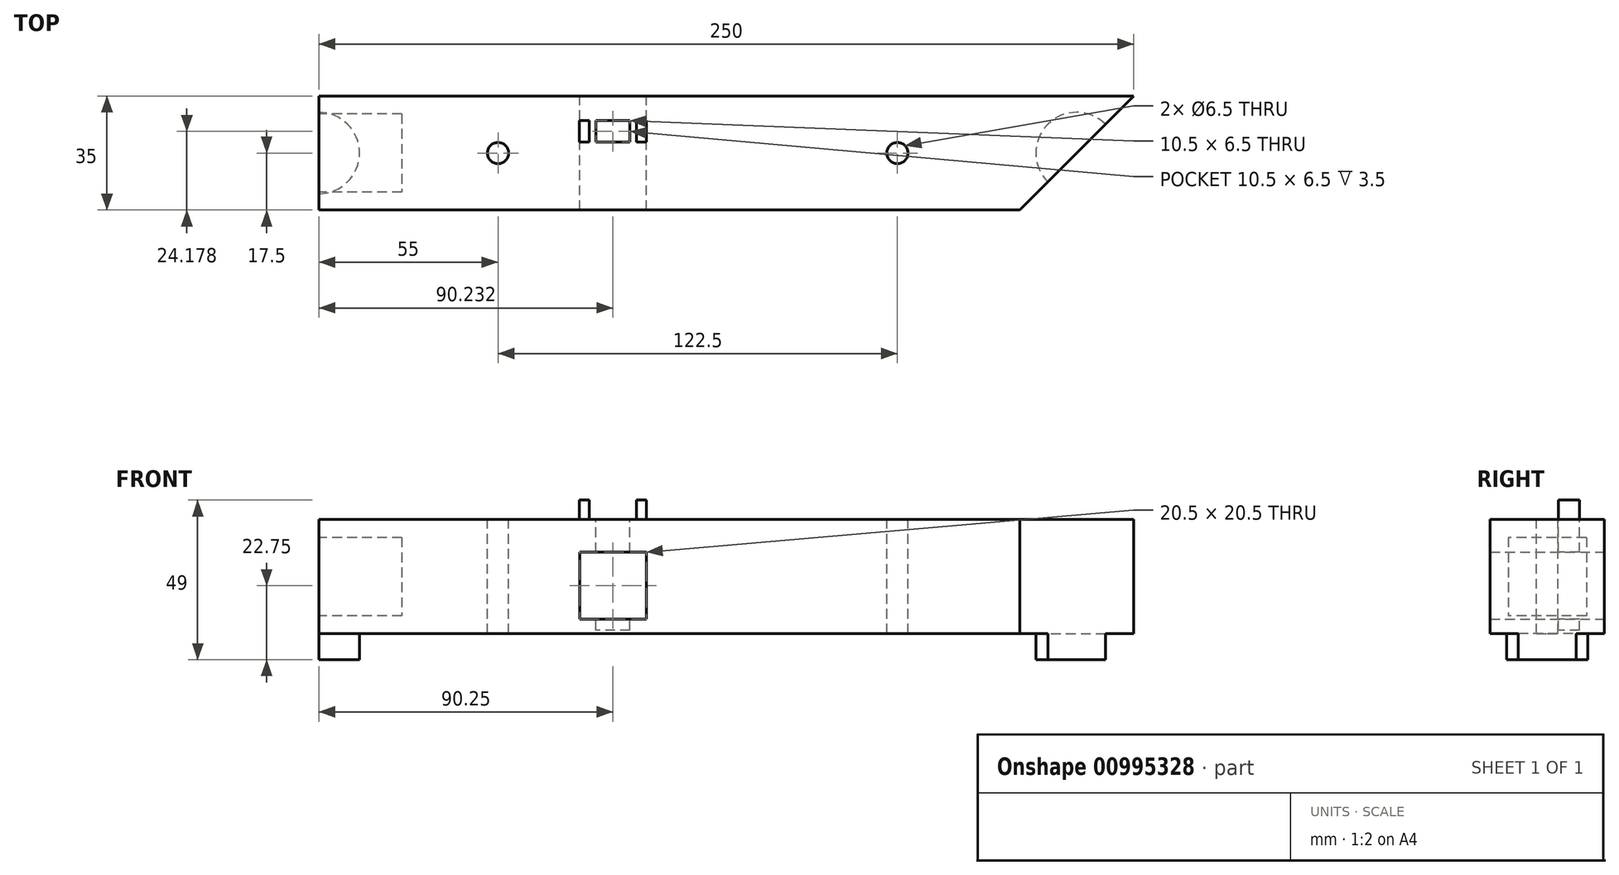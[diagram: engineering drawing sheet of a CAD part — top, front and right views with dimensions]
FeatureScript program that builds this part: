
annotation { "Feature Type Name" : "Feature", "Feature Type Description" : "" }
export const myFeature = defineFeature(function(context is Context, id is Id, definition is map)
    precondition{}
    {
        {
            var Q0;
            Q0=qCreatedBy(makeId("Top.planeOp"),FACE);
            var sketch = newSketch(context, id + "F0", { "sketchPlane" : qUnion([Q0])});
            skLineSegment(sketch, "E0.bottom", {"start": v(125, 17.5) * mm, "end": v(-125, 17.5) * mm});
            skLineSegment(sketch, "E0.top", {"start": v(90, -17.5) * mm, "end": v(-125, -17.5) * mm});
            skLineSegment(sketch, "E0.right", {"start": v(-125, 17.5) * mm, "end": v(-125, -17.5) * mm});
            skPoint(sketch, "E0.middle", {"position": v(0, 0) * mm});
            skPoint(sketch, "E1", {"position": v(90, -17.5) * mm});
            skLineSegment(sketch, "E2", {"start": v(125, 17.5) * mm, "end": v(90, -17.5) * mm});
            skPoint(sketch, "E3.orphan", {"position": v(125, -17.5) * mm});
            skSolve(sketch);
        }
        {
            var Q0;
            Q0=makeQuery(id+"F0.imprint","IMPRINT",FACE,{"disambiguationData":[TD([[makeQuery(id+"F0.imprint","IMPRINT",EDGE,{"derivedFrom":sQuery(id+"F0.wireOp",EDGE,"E0.bottom")}),1.0]])]});
            extrude(context, id + "F1", {"entities" : qUnion([Q0]), "depth" : 35 * mm, "offsetDistance" : 25 * mm});
        }
        {
            var Q0;
            Q0=makeQuery(id+"F1.opExtrude","CAP_FACE",FACE,{"disambiguationData":[OSD([sQuery(id+"F0.wireOp",EDGE,"E0.bottom"),sQuery(id+"F0.wireOp",EDGE,"E0.top"),sQuery(id+"F0.wireOp",EDGE,"E0.right"),sQuery(id+"F0.wireOp",EDGE,"E2")])],"isStart":false});
            var sketch = newSketch(context, id + "F2", { "sketchPlane" : qUnion([Q0])});
            skPoint(sketch, "E4", {"position": v(52.5, 0) * mm});
            skPoint(sketch, "E5", {"position": v(107.5, 0) * mm});
            skPoint(sketch, "E6", {"position": v(-70, 0) * mm});
            skPoint(sketch, "E7", {"position": v(-125, 0) * mm});
            skSolve(sketch);
        }
        {
            var Q0;
            Q0=sQuery(id+"F2.wireOp",VERTEX,"E6");
            var Q1;
            Q1=makeQuery(id+"F1.opExtrude","SWEPT_BODY",BODY,{"disambiguationData":[OSD([sQuery(id+"F0.wireOp",EDGE,"E0.bottom"),sQuery(id+"F0.wireOp",EDGE,"E0.top"),sQuery(id+"F0.wireOp",EDGE,"E0.right"),sQuery(id+"F0.wireOp",EDGE,"E2")])]});
            hole(context, id + "F3", {"style" : HoleStyle.SIMPLE, "endStyle" : HoleEndStyle.BLIND, "holeDiameter" : 6.5 * mm, "majorDiameter" : 5 * mm, "holeDepth" : 35 * mm, "isTappedThrough" : true, "tappedDepth" : 12 * mm, "tapClearance" : 3, "locations" : qUnion([Q0]), "scope" : qUnion([Q1])});
        }
        {
            var Q0;
            Q0=sQuery(id+"F2.wireOp",VERTEX,"E4");
            var Q1;
            Q1=makeQuery(id+"F1.opExtrude","SWEPT_BODY",BODY,{"disambiguationData":[OSD([sQuery(id+"F0.wireOp",EDGE,"E0.bottom"),sQuery(id+"F0.wireOp",EDGE,"E0.top"),sQuery(id+"F0.wireOp",EDGE,"E0.right"),sQuery(id+"F0.wireOp",EDGE,"E2")])]});
            hole(context, id + "F4", {"style" : HoleStyle.SIMPLE, "endStyle" : HoleEndStyle.BLIND, "holeDiameter" : 6.5 * mm, "majorDiameter" : 5 * mm, "holeDepth" : 35 * mm, "isTappedThrough" : true, "tappedDepth" : 12 * mm, "tapClearance" : 3, "locations" : qUnion([Q0]), "scope" : qUnion([Q1])});
        }
        {
            var Q0;
            Q0=makeQuery(id+"F1.opExtrude","SWEPT_FACE",FACE,{"disambiguationData":[OSD([sQuery(id+"F0.wireOp",EDGE,"E0.right")])]});
            var sketch = newSketch(context, id + "F5", { "sketchPlane" : qUnion([Q0])});
            skSolve(sketch);
        }
        {
            var Q0;
            {var subQ0=sQuery(id+"F0.wireOp",EDGE,"E0.right");Q0=makeQuery(id+"F5.imprint","IMPRINT",FACE,{"disambiguationData":[TD([[makeQuery(id+"F5.imprint","IMPRINT",EDGE,{"derivedFrom":makeQuery(id+"F1.opExtrude","CAP_EDGE",EDGE,{"disambiguationData":[OSD([subQ0])],"isStart":true})}),1.0]])]});}
            var sketch = newSketch(context, id + "F6", { "sketchPlane" : qUnion([Q0])});
            skLineSegment(sketch, "E8.0", {"start": v(-12, 5.5) * mm, "end": v(12, 5.5) * mm});
            skLineSegment(sketch, "E8.1", {"start": v(-12, 29.5) * mm, "end": v(-12, 5.5) * mm});
            skLineSegment(sketch, "E9.0", {"start": v(12, 29.5) * mm, "end": v(12, 5.5) * mm});
            skLineSegment(sketch, "E9.1", {"start": v(-12, 29.5) * mm, "end": v(12, 29.5) * mm});
            skSolve(sketch);
        }
        {
            var Q0;
            Q0=makeQuery(id+"F6.imprint","IMPRINT",FACE,{"disambiguationData":[TD([[makeQuery(id+"F6.imprint","IMPRINT",EDGE,{"derivedFrom":sQuery(id+"F6.wireOp",EDGE,"E8.0")}),1.0]])]});
            extrude(context, id + "F7", {"entities" : qUnion([Q0]), "operationType" : NewBodyOperationType.REMOVE, "oppositeDirection" : true, "depth" : 25.5 * mm, "offsetDistance" : 25 * mm});
        }
        {
            var Q0;
            Q0=makeQuery(id+"F1.opExtrude","CAP_FACE",FACE,{"disambiguationData":[OSD([sQuery(id+"F0.wireOp",EDGE,"E0.bottom"),sQuery(id+"F0.wireOp",EDGE,"E0.top"),sQuery(id+"F0.wireOp",EDGE,"E0.right"),sQuery(id+"F0.wireOp",EDGE,"E2")])],"isStart":true});
            var sketch = newSketch(context, id + "F8", { "sketchPlane" : qUnion([Q0])});
            skPoint(sketch, "E10", {"position": v(107.5, 0) * mm});
            skCircle(sketch, "E11", {"center": v(107.5, 0) * mm, "radius": 12.5 * mm});
            skSolve(sketch);
        }
        {
            var Q0;
            {var subQ0=sQuery(id+"F8.wireOp",EDGE,"E11");var subQ1=makeQuery(id+"F1.opExtrude","CAP_EDGE",EDGE,{"disambiguationData":[OSD([sQuery(id+"F0.wireOp",EDGE,"E2")])],"isStart":true});var subQ2=makeQuery(id+"F8.imprint","INTERSECT",VERTEX,{"disambiguationData":[OD(0.0)],"derivedFrom":[subQ1,subQ0]});Q0=makeQuery(id+"F8.imprint","IMPRINT",FACE,{"disambiguationData":[TD([[makeQuery(id+"F8.imprint","IMPRINT",EDGE,{"disambiguationData":[TD([[subQ2,1.0]])],"derivedFrom":subQ0}),1.0]])]});}
            extrude(context, id + "F9", {"entities" : qUnion([Q0]), "operationType" : NewBodyOperationType.ADD, "depth" : 8 * mm, "offsetDistance" : 25 * mm});
        }
        {
            var Q0;
            Q0=makeQuery(id+"F1.opExtrude","CAP_FACE",FACE,{"disambiguationData":[OSD([sQuery(id+"F0.wireOp",EDGE,"E0.bottom"),sQuery(id+"F0.wireOp",EDGE,"E0.top"),sQuery(id+"F0.wireOp",EDGE,"E0.right"),sQuery(id+"F0.wireOp",EDGE,"E2")])],"isStart":true});
            var sketch = newSketch(context, id + "F10", { "sketchPlane" : qUnion([Q0])});
            skCircle(sketch, "E12", {"center": v(-125, 0) * mm, "radius": 12.5 * mm});
            skSolve(sketch);
        }
        {
            var Q0;
            {var subQ0=sQuery(id+"F10.wireOp",EDGE,"E12");var subQ1=makeQuery(id+"F1.opExtrude","CAP_EDGE",EDGE,{"disambiguationData":[OSD([sQuery(id+"F0.wireOp",EDGE,"E0.right")])],"isStart":true});var subQ2=makeQuery(id+"F10.imprint","INTERSECT",VERTEX,{"disambiguationData":[OD(0.0)],"derivedFrom":[subQ1,subQ0]});Q0=makeQuery(id+"F10.imprint","IMPRINT",FACE,{"disambiguationData":[TD([[makeQuery(id+"F10.imprint","IMPRINT",EDGE,{"disambiguationData":[TD([[subQ2,-1.0]])],"derivedFrom":subQ0}),1.0]])]});}
            extrude(context, id + "F11", {"entities" : qUnion([Q0]), "operationType" : NewBodyOperationType.ADD, "depth" : 8 * mm, "offsetDistance" : 25 * mm});
        }
        {
            var Q0;
            Q0=makeQuery(id+"F1.opExtrude","SWEPT_FACE",FACE,{"disambiguationData":[OSD([sQuery(id+"F0.wireOp",EDGE,"E0.bottom")])]});
            var sketch = newSketch(context, id + "F12", { "sketchPlane" : qUnion([Q0])});
            skPoint(sketch, "E13", {"position": v(45, 25) * mm});
            skLineSegment(sketch, "E14.bottom", {"start": v(45, 25) * mm, "end": v(24.5, 25) * mm});
            skLineSegment(sketch, "E14.top", {"start": v(45, 4.5) * mm, "end": v(24.5, 4.5) * mm});
            skLineSegment(sketch, "E14.left", {"start": v(45, 25) * mm, "end": v(45, 4.5) * mm});
            skLineSegment(sketch, "E14.right", {"start": v(24.5, 25) * mm, "end": v(24.5, 4.5) * mm});
            skPoint(sketch, "E15", {"position": v(24.5, 35) * mm});
            skPoint(sketch, "E16", {"position": v(45, 35) * mm});
            skSolve(sketch);
        }
        {
            var Q0;
            Q0=makeQuery(id+"F12.imprint","IMPRINT",FACE,{"disambiguationData":[TD([[makeQuery(id+"F12.imprint","IMPRINT",EDGE,{"derivedFrom":sQuery(id+"F12.wireOp",EDGE,"E14.bottom")}),1.0]])]});
            var Q1;
            Q1=sQuery(id+"F12.wireOp",EDGE,"E14.bottom");
            extrude(context, id + "F13", {"entities" : qUnion([Q0]), "operationType" : NewBodyOperationType.REMOVE, "surfaceEntities" : qUnion([Q1]), "oppositeDirection" : true, "depth" : 100 * mm, "offsetDistance" : 25 * mm});
        }
        {
            var Q0;
            Q0=makeQuery(id+"F1.opExtrude","CAP_FACE",FACE,{"disambiguationData":[OSD([sQuery(id+"F0.wireOp",EDGE,"E0.bottom"),sQuery(id+"F0.wireOp",EDGE,"E0.top"),sQuery(id+"F0.wireOp",EDGE,"E0.right"),sQuery(id+"F0.wireOp",EDGE,"E2")])],"isStart":false});
            var sketch = newSketch(context, id + "F14", { "sketchPlane" : qUnion([Q0])});
            skPoint(sketch, "E17", {"position": v(-16.28, 97.92) * mm});
            skPoint(sketch, "E18", {"position": v(-24.54, 17.5) * mm});
            skPoint(sketch, "E19", {"position": v(-8.69, 103.63) * mm});
            skPoint(sketch, "E20", {"position": v(-45, 17.5) * mm});
            skPoint(sketch, "E21", {"position": v(17.73, 139.2) * mm});
            skPoint(sketch, "E22", {"position": v(-71.08, 32.76) * mm});
            skPoint(sketch, "E23", {"position": v(-45, -9.93) * mm});
            skPoint(sketch, "E24", {"position": v(-24.54, -9.93) * mm});
            skPoint(sketch, "E25", {"position": v(-45, 59.26) * mm});
            skLineSegment(sketch, "E26", {"start": v(-45, -9.93) * mm, "end": v(-24.54, -9.93) * mm});
            skPoint(sketch, "E27", {"position": v(-34.77, -9.93) * mm});
            skPoint(sketch, "E28", {"position": v(-15.54, 62.05) * mm});
            skPoint(sketch, "E29", {"position": v(-29.52, -9.93) * mm});
            skPoint(sketch, "E30", {"position": v(-40.02, -9.93) * mm});
            skLineSegment(sketch, "E31.bottom", {"start": v(-29.52, -9.93) * mm, "end": v(-40.02, -9.93) * mm});
            skLineSegment(sketch, "E31.top", {"start": v(-29.52, -3.43) * mm, "end": v(-40.02, -3.43) * mm});
            skLineSegment(sketch, "E31.left", {"start": v(-29.52, -9.93) * mm, "end": v(-29.52, -3.43) * mm});
            skLineSegment(sketch, "E31.right", {"start": v(-40.02, -9.93) * mm, "end": v(-40.02, -3.43) * mm});
            skLineSegment(sketch, "E32", {"start": v(-47.6, 0) * mm, "end": v(-17.1, 0) * mm});
            skLineSegment(sketch, "E33.MirrorCS", {"start": v(-29.52, 3.43) * mm, "end": v(-40.02, 3.43) * mm});
            skLineSegment(sketch, "E34.MirrorCS", {"start": v(-40.02, 9.93) * mm, "end": v(-40.02, 3.43) * mm});
            skLineSegment(sketch, "E35.MirrorCS", {"start": v(-29.52, 9.93) * mm, "end": v(-29.52, 3.43) * mm});
            skLineSegment(sketch, "E36.MirrorCS", {"start": v(-29.52, 9.93) * mm, "end": v(-40.02, 9.93) * mm});
            skSolve(sketch);
        }
        {
            var Q0;
            Q0=makeQuery(id+"F1.opExtrude","CAP_FACE",FACE,{"disambiguationData":[OSD([sQuery(id+"F0.wireOp",EDGE,"E0.bottom"),sQuery(id+"F0.wireOp",EDGE,"E0.top"),sQuery(id+"F0.wireOp",EDGE,"E0.right"),sQuery(id+"F0.wireOp",EDGE,"E2")])],"isStart":false});
            var sketch = newSketch(context, id + "F15", { "sketchPlane" : qUnion([Q0])});
            skPoint(sketch, "E37", {"position": v(-27.52, -3.43) * mm});
            skPoint(sketch, "E38", {"position": v(-24.52, -9.93) * mm});
            skPoint(sketch, "E39", {"position": v(-45.02, -9.93) * mm});
            skPoint(sketch, "E40", {"position": v(-42.02, -3.43) * mm});
            skLineSegment(sketch, "E41.bottom", {"start": v(-45.02, -9.93) * mm, "end": v(-42.02, -9.93) * mm});
            skLineSegment(sketch, "E41.top", {"start": v(-45.02, -3.43) * mm, "end": v(-42.02, -3.43) * mm});
            skLineSegment(sketch, "E41.left", {"start": v(-45.02, -9.93) * mm, "end": v(-45.02, -3.43) * mm});
            skLineSegment(sketch, "E41.right", {"start": v(-42.02, -9.93) * mm, "end": v(-42.02, -3.43) * mm});
            skLineSegment(sketch, "E42.bottom", {"start": v(-27.52, -3.43) * mm, "end": v(-24.52, -3.43) * mm});
            skLineSegment(sketch, "E42.top", {"start": v(-27.52, -9.93) * mm, "end": v(-24.52, -9.93) * mm});
            skLineSegment(sketch, "E42.left", {"start": v(-27.52, -3.43) * mm, "end": v(-27.52, -9.93) * mm});
            skLineSegment(sketch, "E42.right", {"start": v(-24.52, -3.43) * mm, "end": v(-24.52, -9.93) * mm});
            skLineSegment(sketch, "E43", {"start": v(-51.35, 0) * mm, "end": v(-20.65, 0) * mm});
            skLineSegment(sketch, "E44.MirrorCS", {"start": v(-45.02, 3.43) * mm, "end": v(-42.02, 3.43) * mm});
            skLineSegment(sketch, "E45.MirrorCS", {"start": v(-45.02, 9.93) * mm, "end": v(-45.02, 3.43) * mm});
            skLineSegment(sketch, "E46.MirrorCS", {"start": v(-42.02, 9.93) * mm, "end": v(-42.02, 3.43) * mm});
            skLineSegment(sketch, "E47.MirrorCS", {"start": v(-45.02, 9.93) * mm, "end": v(-42.02, 9.93) * mm});
            skLineSegment(sketch, "E48.MirrorCS", {"start": v(-27.52, 3.43) * mm, "end": v(-27.52, 9.93) * mm});
            skLineSegment(sketch, "E49.MirrorCS", {"start": v(-27.52, 3.43) * mm, "end": v(-24.52, 3.43) * mm});
            skLineSegment(sketch, "E50.MirrorCS", {"start": v(-24.52, 3.43) * mm, "end": v(-24.52, 9.93) * mm});
            skLineSegment(sketch, "E51.MirrorCS", {"start": v(-27.52, 9.93) * mm, "end": v(-24.52, 9.93) * mm});
            skSolve(sketch);
        }
        {
            var Q0;
            Q0=makeQuery(id+"F14.imprint","IMPRINT",FACE,{"disambiguationData":[TD([[makeQuery(id+"F14.imprint","IMPRINT",EDGE,{"derivedFrom":sQuery(id+"F14.wireOp",EDGE,"E33.MirrorCS")}),-1.0]])]});
            extrude(context, id + "F16", {"entities" : qUnion([Q0]), "operationType" : NewBodyOperationType.REMOVE, "oppositeDirection" : true, "depth" : 34 * mm, "offsetDistance" : 25 * mm});
        }
        {
            var Q0;
            Q0=makeQuery(id+"F15.imprint","IMPRINT",FACE,{"disambiguationData":[TD([[makeQuery(id+"F15.imprint","IMPRINT",EDGE,{"derivedFrom":sQuery(id+"F15.wireOp",EDGE,"E44.MirrorCS")}),1.0]])]});
            var Q1;
            Q1=makeQuery(id+"F15.imprint","IMPRINT",FACE,{"disambiguationData":[TD([[makeQuery(id+"F15.imprint","IMPRINT",EDGE,{"derivedFrom":sQuery(id+"F15.wireOp",EDGE,"E48.MirrorCS")}),-1.0]])]});
            extrude(context, id + "F17", {"entities" : qUnion([Q0, Q1]), "operationType" : NewBodyOperationType.ADD, "depth" : 6 * mm, "offsetDistance" : 25 * mm});
        }
    });
